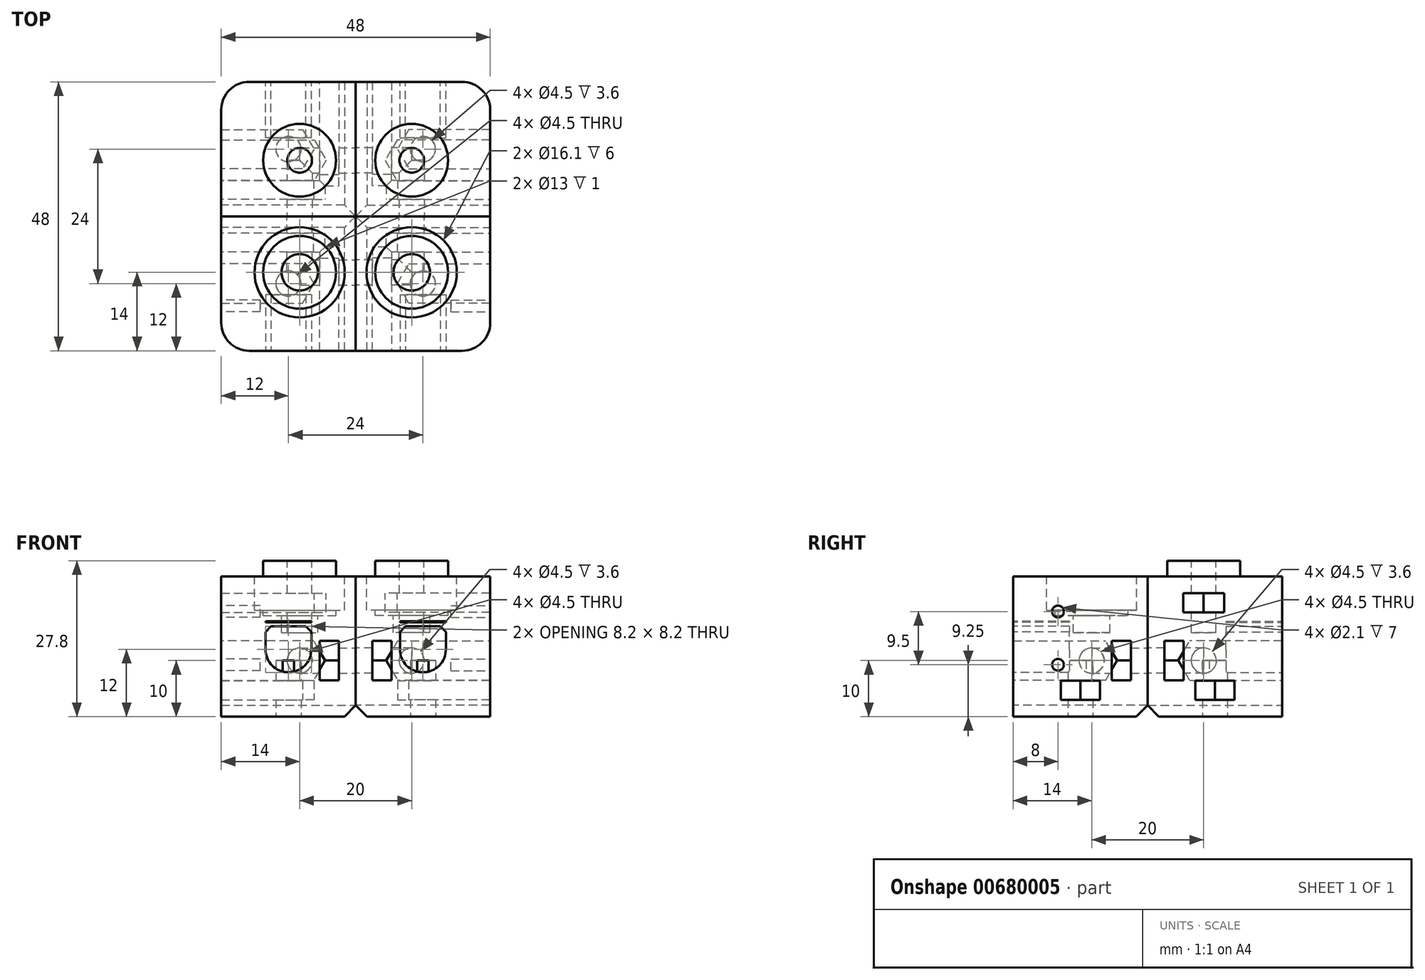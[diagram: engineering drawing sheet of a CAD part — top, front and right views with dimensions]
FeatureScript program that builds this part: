
annotation { "Feature Type Name" : "Feature", "Feature Type Description" : "" }
export const myFeature = defineFeature(function(context is Context, id is Id, definition is map)
    precondition{}
    {
        {
            var Q0;
            Q0=qCreatedBy(makeId("Top.planeOp"),FACE);
            var sketch = newSketch(context, id + "F0", { "sketchPlane" : qUnion([Q0])});
            skLineSegment(sketch, "E0.bottom", {"start": v(0, 0) * mm, "end": v(24, 0) * mm});
            skLineSegment(sketch, "E0.top", {"start": v(0, -24) * mm, "end": v(24, -24) * mm});
            skLineSegment(sketch, "E0.left", {"start": v(0, 0) * mm, "end": v(0, -24) * mm});
            skLineSegment(sketch, "E0.right", {"start": v(24, 0) * mm, "end": v(24, -24) * mm});
            skCircle(sketch, "E1", {"center": v(12, -12) * mm, "radius": 2.25 * mm});
            skLineSegment(sketch, "E2.3", {"start": v(9.48, -15.5) * mm, "end": v(7.46, -12) * mm});
            skLineSegment(sketch, "E2.4", {"start": v(7.46, -12) * mm, "end": v(9.48, -8.5) * mm});
            skLineSegment(sketch, "E3", {"start": v(24, -8.5) * mm, "end": v(24, -15.5) * mm});
            skLineSegment(sketch, "E4", {"start": v(9.48, -8.5) * mm, "end": v(24, -8.5) * mm});
            skLineSegment(sketch, "E5", {"start": v(24, -15.5) * mm, "end": v(9.48, -15.5) * mm});
            skLineSegment(sketch, "E6", {"start": v(8.47, -13.75) * mm, "end": v(11.5, -12) * mm, "construction": true});
            skLineSegment(sketch, "E7", {"start": v(11.5, -12) * mm, "end": v(12, -12) * mm, "construction": true});
            skLineSegment(sketch, "E8", {"start": v(7.46, -12) * mm, "end": v(11.5, -12) * mm, "construction": true});
            skSolve(sketch);
        }
        {
            var Q0;
            Q0=qSketchRegion(id+"F0",true);
            var Q1;
            Q1=makeQuery(id+"F0.imprint","IMPRINT",FACE,{"disambiguationData":[TD([[makeQuery(id+"F0.imprint","IMPRINT",EDGE,{"derivedFrom":sQuery(id+"F0.wireOp",EDGE,"E1")}),-1.0]])]});
            var Q2;
            Q2=makeQuery(id+"F0.imprint","IMPRINT",FACE,{"disambiguationData":[TD([[makeQuery(id+"F0.imprint","IMPRINT",EDGE,{"derivedFrom":sQuery(id+"F0.wireOp",EDGE,"E1")}),1.0]])]});
            extrude(context, id + "F1", {"entities" : qUnion([Q0, Q1, Q2]), "depth" : 25 * mm});
        }
        {
            var Q0;
            Q0=makeQuery(id+"F0.imprint","IMPRINT",FACE,{"disambiguationData":[TD([[makeQuery(id+"F0.imprint","IMPRINT",EDGE,{"derivedFrom":sQuery(id+"F0.wireOp",EDGE,"E1")}),1.0]])]});
            extrude(context, id + "F2", {"entities" : qUnion([Q0]), "operationType" : NewBodyOperationType.REMOVE, "depth" : 10 * mm});
        }
        {
            var Q0;
            Q0=makeQuery(id+"F0.imprint","IMPRINT",FACE,{"disambiguationData":[TD([[makeQuery(id+"F0.imprint","IMPRINT",EDGE,{"derivedFrom":sQuery(id+"F0.wireOp",EDGE,"E2.0")}),1.0]])]});
            var Q1;
            Q1=makeQuery(id+"F0.imprint","IMPRINT",FACE,{"disambiguationData":[TD([[makeQuery(id+"F0.imprint","IMPRINT",EDGE,{"derivedFrom":sQuery(id+"F0.wireOp",EDGE,"E1")}),-1.0]])]});
            extrude(context, id + "F3", {"entities" : qUnion([Q0, Q1]), "operationType" : NewBodyOperationType.REMOVE, "depth" : 3 * mm + 3.4 * mm});
        }
        {
            var Q0;
            Q0=makeQuery(id+"F0.imprint","IMPRINT",FACE,{"disambiguationData":[TD([[makeQuery(id+"F0.imprint","IMPRINT",EDGE,{"derivedFrom":sQuery(id+"F0.wireOp",EDGE,"E1")}),-1.0]])]});
            var Q1;
            Q1=makeQuery(id+"F0.imprint","IMPRINT",FACE,{"disambiguationData":[TD([[makeQuery(id+"F0.imprint","IMPRINT",EDGE,{"derivedFrom":sQuery(id+"F0.wireOp",EDGE,"E2.0")}),1.0]])]});
            extrude(context, id + "F4", {"entities" : qUnion([Q0, Q1]), "operationType" : NewBodyOperationType.ADD, "depth" : 3 * mm});
        }
        {
            var Q0;
            Q0=makeQuery(id+"F1.opExtrude","SWEPT_FACE",FACE,{"disambiguationData":[OSD([sQuery(id+"F0.wireOp",EDGE,"E0.top")])]});
            var sketch = newSketch(context, id + "F5", { "sketchPlane" : qUnion([Q0])});
            skCircle(sketch, "E9", {"center": v(12, 12) * mm, "radius": 4 * mm});
            skLineSegment(sketch, "E10", {"start": v(8.72, 14.3) * mm, "end": v(10.76, 17.2) * mm});
            skLineSegment(sketch, "E11", {"start": v(10.76, 17.2) * mm, "end": v(13.24, 17.2) * mm});
            skLineSegment(sketch, "E12", {"start": v(13.24, 17.2) * mm, "end": v(15.28, 14.3) * mm});
            skSolve(sketch);
        }
        {
            var Q0;
            {var subQ1=sQuery(id+"F5.wireOp",EDGE,"E10");Q0=makeQuery(id+"F5.imprint","IMPRINT",FACE,{"disambiguationData":[TD([[makeQuery(id+"F5.imprint","IMPRINT",EDGE,{"derivedFrom":subQ1}),1.0]])]});}
            var sketch = newSketch(context, id + "F6", { "sketchPlane" : qUnion([Q0])});
            skCircle(sketch, "E13", {"center": v(12, 12) * mm, "radius": 4.1 * mm});
            skLineSegment(sketch, "E14", {"start": v(16.1, 12) * mm, "end": v(16.1, 16.1) * mm, "construction": true});
            skLineSegment(sketch, "E15", {"start": v(16.1, 16.1) * mm, "end": v(7.9, 16.1) * mm});
            skLineSegment(sketch, "E16", {"start": v(7.9, 16.1) * mm, "end": v(7.9, 12) * mm, "construction": true});
            skLineSegment(sketch, "E17", {"start": v(7.9, 16.1) * mm, "end": v(7.9, 17) * mm, "construction": true});
            skLineSegment(sketch, "E18", {"start": v(7.9, 17) * mm, "end": v(7.9, 16.8) * mm});
            skLineSegment(sketch, "E19", {"start": v(7.9, 16.8) * mm, "end": v(16.1, 16.8) * mm});
            skLineSegment(sketch, "E20", {"start": v(16.1, 16.8) * mm, "end": v(16.1, 17) * mm});
            skLineSegment(sketch, "E21", {"start": v(16.1, 17) * mm, "end": v(7.9, 17) * mm});
            skLineSegment(sketch, "E22", {"start": v(15.1, 16.1) * mm, "end": v(16.1, 15.1) * mm});
            skLineSegment(sketch, "E23", {"start": v(16.1, 15.1) * mm, "end": v(16.1, 12) * mm});
            skLineSegment(sketch, "E24", {"start": v(7.9, 12) * mm, "end": v(7.9, 15.1) * mm});
            skLineSegment(sketch, "E25", {"start": v(7.9, 15.1) * mm, "end": v(8.9, 16.1) * mm});
            skSolve(sketch);
        }
        {
            var Q0;
            Q0=qSketchRegion(id+"F6",true);
            extrude(context, id + "F7", {"entities" : qUnion([Q0]), "operationType" : NewBodyOperationType.REMOVE, "oppositeDirection" : true, "depth" : 10 * mm});
        }
        {
            var Q0;
            Q0=makeQuery(id+"F1.opExtrude","SWEPT_FACE",FACE,{"disambiguationData":[OSD([sQuery(id+"F0.wireOp",EDGE,"E0.left")])]});
            var sketch = newSketch(context, id + "F8", { "sketchPlane" : qUnion([Q0])});
            skCircle(sketch, "E26", {"center": v(10, 10) * mm, "radius": 2.25 * mm});
            skLineSegment(sketch, "E27.3", {"start": v(7.48, 6.5) * mm, "end": v(5.46, 10) * mm});
            skLineSegment(sketch, "E27.4", {"start": v(5.46, 10) * mm, "end": v(7.48, 13.5) * mm});
            skLineSegment(sketch, "E28", {"start": v(24, 6.5) * mm, "end": v(24, 13.5) * mm});
            skLineSegment(sketch, "E29", {"start": v(24, 13.5) * mm, "end": v(7.48, 13.5) * mm});
            skLineSegment(sketch, "E30", {"start": v(7.48, 6.5) * mm, "end": v(24, 6.5) * mm});
            skLineSegment(sketch, "E31", {"start": v(10, 13.5) * mm, "end": v(10, 6.5) * mm, "construction": true});
            skLineSegment(sketch, "E32", {"start": v(6.47, 11.75) * mm, "end": v(9.5, 10) * mm, "construction": true});
            skLineSegment(sketch, "E33", {"start": v(9.5, 10) * mm, "end": v(10, 10) * mm, "construction": true});
            skSolve(sketch);
        }
        {
            var Q0;
            Q0=makeQuery(id+"F8.imprint","IMPRINT",FACE,{"disambiguationData":[TD([[makeQuery(id+"F8.imprint","IMPRINT",EDGE,{"derivedFrom":sQuery(id+"F8.wireOp",EDGE,"E26")}),1.0]])]});
            extrude(context, id + "F9", {"entities" : qUnion([Q0]), "operationType" : NewBodyOperationType.REMOVE, "oppositeDirection" : true, "depth" : 10 * mm});
        }
        {
            var Q0;
            Q0=makeQuery(id+"F8.imprint","IMPRINT",FACE,{"disambiguationData":[TD([[makeQuery(id+"F8.imprint","IMPRINT",EDGE,{"derivedFrom":sQuery(id+"F8.wireOp",EDGE,"E26")}),-1.0]])]});
            var Q1;
            Q1=makeQuery(id+"F8.imprint","IMPRINT",FACE,{"disambiguationData":[TD([[makeQuery(id+"F8.imprint","IMPRINT",EDGE,{"derivedFrom":sQuery(id+"F8.wireOp",EDGE,"E27.0")}),1.0]])]});
            extrude(context, id + "F10", {"entities" : qUnion([Q0, Q1]), "operationType" : NewBodyOperationType.REMOVE, "oppositeDirection" : true, "depth" : 3 * mm + 3.4 * mm});
        }
        {
            var Q0;
            Q0=makeQuery(id+"F8.imprint","IMPRINT",FACE,{"disambiguationData":[TD([[makeQuery(id+"F8.imprint","IMPRINT",EDGE,{"derivedFrom":sQuery(id+"F8.wireOp",EDGE,"E26")}),-1.0]])]});
            var Q1;
            Q1=makeQuery(id+"F8.imprint","IMPRINT",FACE,{"disambiguationData":[TD([[makeQuery(id+"F8.imprint","IMPRINT",EDGE,{"derivedFrom":sQuery(id+"F8.wireOp",EDGE,"E27.0")}),1.0]])]});
            extrude(context, id + "F11", {"entities" : qUnion([Q0, Q1]), "operationType" : NewBodyOperationType.ADD, "oppositeDirection" : true, "depth" : 3 * mm});
        }
        {
            var Q0;
            Q0=makeQuery(id+"F1.opExtrude","SWEPT_FACE",FACE,{"disambiguationData":[OSD([sQuery(id+"F0.wireOp",EDGE,"E0.bottom")])]});
            var sketch = newSketch(context, id + "F12", { "sketchPlane" : qUnion([Q0])});
            skCircle(sketch, "E34", {"center": v(-10, 10) * mm, "radius": 2.25 * mm});
            skLineSegment(sketch, "E35.0", {"start": v(-7.48, 13.5) * mm, "end": v(-5.46, 10) * mm});
            skLineSegment(sketch, "E35.1", {"start": v(-5.46, 10) * mm, "end": v(-7.48, 6.5) * mm});
            skPoint(sketch, "E35.0.midPoint", {"position": v(-6.47, 11.75) * mm});
            skLineSegment(sketch, "E36", {"start": v(-24, 13.5) * mm, "end": v(-24, 6.5) * mm});
            skLineSegment(sketch, "E37", {"start": v(-7.48, 13.5) * mm, "end": v(-24, 13.5) * mm});
            skLineSegment(sketch, "E38", {"start": v(-24, 6.5) * mm, "end": v(-7.48, 6.5) * mm});
            skLineSegment(sketch, "E39", {"start": v(-10, 13.5) * mm, "end": v(-10, 6.5) * mm, "construction": true});
            skLineSegment(sketch, "E40", {"start": v(-6.47, 11.75) * mm, "end": v(-9.5, 10) * mm});
            skLineSegment(sketch, "E41", {"start": v(-9.5, 10) * mm, "end": v(-10, 10) * mm});
            skSolve(sketch);
        }
        {
            var Q0;
            Q0=makeQuery(id+"F12.imprint","IMPRINT",FACE,{"disambiguationData":[TD([[makeQuery(id+"F12.imprint","IMPRINT",EDGE,{"derivedFrom":sQuery(id+"F12.wireOp",EDGE,"E34")}),1.0]])]});
            extrude(context, id + "F13", {"entities" : qUnion([Q0]), "operationType" : NewBodyOperationType.REMOVE, "oppositeDirection" : true, "depth" : 10 * mm});
        }
        {
            var Q0;
            Q0=makeQuery(id+"F12.imprint","IMPRINT",FACE,{"disambiguationData":[TD([[makeQuery(id+"F12.imprint","IMPRINT",EDGE,{"derivedFrom":sQuery(id+"F12.wireOp",EDGE,"E35.3")}),1.0]])]});
            var Q1;
            Q1=makeQuery(id+"F12.imprint","IMPRINT",FACE,{"disambiguationData":[TD([[makeQuery(id+"F12.imprint","IMPRINT",EDGE,{"derivedFrom":sQuery(id+"F12.wireOp",EDGE,"E34")}),-1.0]])]});
            extrude(context, id + "F14", {"entities" : qUnion([Q0, Q1]), "operationType" : NewBodyOperationType.REMOVE, "oppositeDirection" : true, "depth" : 3 * mm + 3.4 * mm});
        }
        {
            var Q0;
            Q0=makeQuery(id+"F12.imprint","IMPRINT",FACE,{"disambiguationData":[TD([[makeQuery(id+"F12.imprint","IMPRINT",EDGE,{"derivedFrom":sQuery(id+"F12.wireOp",EDGE,"E35.3")}),1.0]])]});
            var Q1;
            Q1=makeQuery(id+"F12.imprint","IMPRINT",FACE,{"disambiguationData":[TD([[makeQuery(id+"F12.imprint","IMPRINT",EDGE,{"derivedFrom":sQuery(id+"F12.wireOp",EDGE,"E34")}),-1.0]])]});
            extrude(context, id + "F15", {"entities" : qUnion([Q0, Q1]), "operationType" : NewBodyOperationType.ADD, "oppositeDirection" : true, "depth" : 3 * mm});
        }
        {
            var Q0;
            Q0=makeQuery(id+"F1.opExtrude","SWEPT_EDGE",EDGE,{"disambiguationData":[OSD([sQuery(id+"F0.wireOp",EDGE,"E0.top"),sQuery(id+"F0.wireOp",EDGE,"E0.right")])]});
            fillet(context, id + "F16", {"entities" : qUnion([Q0]), "radius" : 5 * mm, "tangentPropagation" : true, "allowEdgeOverflow" : false});
        }
        {
            var Q0;
            Q0=makeQuery(id+"F1.opExtrude","CAP_EDGE",EDGE,{"disambiguationData":[OSD([sQuery(id+"F0.wireOp",EDGE,"E0.left")])],"isStart":true});
            var Q1;
            Q1=makeQuery(id+"F1.opExtrude","CAP_EDGE",EDGE,{"disambiguationData":[OSD([sQuery(id+"F0.wireOp",EDGE,"E0.bottom")])],"isStart":true});
            chamfer(context, id + "F17", {"entities" : qUnion([Q0, Q1]), "width" : 2 * mm, "tangentPropagation" : true});
        }
        {
            var Q0;
            Q0=makeQuery(id+"F1.opExtrude","SWEPT_BODY",BODY,{"disambiguationData":[OSD([sQuery(id+"F0.wireOp",EDGE,"E0.bottom"),sQuery(id+"F0.wireOp",EDGE,"E0.top"),sQuery(id+"F0.wireOp",EDGE,"E0.left"),sQuery(id+"F0.wireOp",EDGE,"E0.right"),sQuery(id+"F0.wireOp",EDGE,"E3")])]});
            var Q1;
            Q1=qCreatedBy(makeId("Front.planeOp"),FACE);
            mirror(context, id + "F18", {"entities" : qUnion([Q0]), "mirrorPlane" : qUnion([Q1])});
        }
        {
            var Q0;
            Q0=makeQuery(id+"F18.opPattern","COPY",FACE,{"derivedFrom":makeQuery(id+"F1.opExtrude","CAP_FACE",FACE,{"disambiguationData":[OSD([sQuery(id+"F0.wireOp",EDGE,"E0.bottom"),sQuery(id+"F0.wireOp",EDGE,"E0.top"),sQuery(id+"F0.wireOp",EDGE,"E0.left"),sQuery(id+"F0.wireOp",EDGE,"E0.right"),sQuery(id+"F0.wireOp",EDGE,"E3")])],"isStart":false}),"instanceName":"1"});
            var sketch = newSketch(context, id + "F19", { "sketchPlane" : qUnion([Q0])});
            skCircle(sketch, "E42", {"center": v(10, 10) * mm, "radius": 2.2 * mm});
            skCircle(sketch, "E43", {"center": v(10, 10) * mm, "radius": 6.5 * mm});
            skLineSegment(sketch, "E44", {"start": v(24, 13.65) * mm, "end": v(24, 6.35) * mm});
            skLineSegment(sketch, "E45", {"start": v(24, 13.65) * mm, "end": v(7.4, 13.65) * mm});
            skLineSegment(sketch, "E46", {"start": v(7.4, 13.65) * mm, "end": v(5.29, 10) * mm});
            skLineSegment(sketch, "E47", {"start": v(5.29, 10) * mm, "end": v(7.4, 6.35) * mm});
            skLineSegment(sketch, "E48", {"start": v(7.4, 6.35) * mm, "end": v(24, 6.35) * mm});
            skLineSegment(sketch, "E49", {"start": v(6.34, 11.83) * mm, "end": v(9.5, 10) * mm, "construction": true});
            skLineSegment(sketch, "E50", {"start": v(9.5, 10) * mm, "end": v(10, 10) * mm, "construction": true});
            skLineSegment(sketch, "E51", {"start": v(5.29, 10) * mm, "end": v(9.5, 10) * mm, "construction": true});
            skSolve(sketch);
        }
        {
            var Q0;
            Q0=makeQuery(id+"F19.imprint","IMPRINT",FACE,{"disambiguationData":[TD([[makeQuery(id+"F19.imprint","IMPRINT",EDGE,{"derivedFrom":sQuery(id+"F19.wireOp",EDGE,"E42")}),1.0]])]});
            extrude(context, id + "F20", {"entities" : qUnion([Q0]), "operationType" : NewBodyOperationType.REMOVE, "oppositeDirection" : true, "depth" : 10 * mm});
        }
        {
            var Q0;
            {var subQ6=sQuery(id+"F19.wireOp",EDGE,"3c2f8247-9d55-409e-9478-93798bc3c1df.1");Q0=makeQuery(id+"F19.imprint","IMPRINT",FACE,{"disambiguationData":[TD([[makeQuery(id+"F19.imprint","IMPRINT",EDGE,{"derivedFrom":subQ6}),1.0]])]});}
            var Q1;
            {var subQ4=sQuery(id+"F19.wireOp",EDGE,"E44");Q1=makeQuery(id+"F19.imprint","IMPRINT",FACE,{"disambiguationData":[TD([[makeQuery(id+"F19.imprint","IMPRINT",EDGE,{"derivedFrom":subQ4}),1.0]])]});}
            var Q2;
            Q2=makeQuery(id+"F19.imprint","IMPRINT",FACE,{"disambiguationData":[TD([[makeQuery(id+"F19.imprint","IMPRINT",EDGE,{"derivedFrom":sQuery(id+"F19.wireOp",EDGE,"E42")}),-1.0]])]});
            extrude(context, id + "F21", {"entities" : qUnion([Q0, Q1, Q2]), "operationType" : NewBodyOperationType.REMOVE, "oppositeDirection" : true, "depth" : 3 * mm + 3.4 * mm});
        }
        {
            var Q0;
            Q0=makeQuery(id+"F19.imprint","IMPRINT",FACE,{"disambiguationData":[TD([[makeQuery(id+"F19.imprint","IMPRINT",EDGE,{"derivedFrom":sQuery(id+"F19.wireOp",EDGE,"E42")}),-1.0]])]});
            var Q1;
            {var subQ4=sQuery(id+"F19.wireOp",EDGE,"E44");Q1=makeQuery(id+"F19.imprint","IMPRINT",FACE,{"disambiguationData":[TD([[makeQuery(id+"F19.imprint","IMPRINT",EDGE,{"derivedFrom":subQ4}),1.0]])]});}
            var Q2;
            {var subQ6=sQuery(id+"F19.wireOp",EDGE,"3c2f8247-9d55-409e-9478-93798bc3c1df.1");Q2=makeQuery(id+"F19.imprint","IMPRINT",FACE,{"disambiguationData":[TD([[makeQuery(id+"F19.imprint","IMPRINT",EDGE,{"derivedFrom":subQ6}),1.0]])]});}
            extrude(context, id + "F22", {"entities" : qUnion([Q0, Q1, Q2]), "operationType" : NewBodyOperationType.ADD, "oppositeDirection" : true, "depth" : 3 * mm});
        }
        {
            var Q0;
            {var subQ4=sQuery(id+"F19.wireOp",EDGE,"E46");Q0=makeQuery(id+"F19.imprint","IMPRINT",FACE,{"disambiguationData":[TD([[makeQuery(id+"F19.imprint","IMPRINT",EDGE,{"derivedFrom":subQ4}),-1.0]])]});}
            var Q1;
            Q1=makeQuery(id+"F19.imprint","IMPRINT",FACE,{"disambiguationData":[TD([[makeQuery(id+"F19.imprint","IMPRINT",EDGE,{"derivedFrom":sQuery(id+"F19.wireOp",EDGE,"E42")}),-1.0]])]});
            extrude(context, id + "F23", {"entities" : qUnion([Q0, Q1]), "operationType" : NewBodyOperationType.ADD, "depth" : 16 * mm + 12 * mm - 25 * mm - .2 * mm});
        }
        {
            var Q0;
            Q0=makeQuery(id+"F1.opExtrude","CAP_FACE",FACE,{"disambiguationData":[OSD([sQuery(id+"F0.wireOp",EDGE,"E0.bottom"),sQuery(id+"F0.wireOp",EDGE,"E0.top"),sQuery(id+"F0.wireOp",EDGE,"E0.left"),sQuery(id+"F0.wireOp",EDGE,"E0.right")])],"isStart":false});
            var sketch = newSketch(context, id + "F24", { "sketchPlane" : qUnion([Q0])});
            skCircle(sketch, "E52", {"center": v(10, -10) * mm, "radius": 3.25 * mm});
            skCircle(sketch, "E53", {"center": v(10, -10) * mm, "radius": 8.05 * mm});
            skCircle(sketch, "E54", {"center": v(10, -10) * mm, "radius": 6.5 * mm});
            skSolve(sketch);
        }
        {
            var Q0;
            Q0=makeQuery(id+"F24.imprint","IMPRINT",FACE,{"disambiguationData":[TD([[makeQuery(id+"F24.imprint","IMPRINT",EDGE,{"derivedFrom":sQuery(id+"F24.wireOp",EDGE,"E52")}),1.0]])]});
            extrude(context, id + "F25", {"entities" : qUnion([Q0]), "operationType" : NewBodyOperationType.REMOVE, "oppositeDirection" : true, "depth" : 10 * mm});
        }
        {
            var Q0;
            Q0=makeQuery(id+"F24.imprint","IMPRINT",FACE,{"disambiguationData":[TD([[makeQuery(id+"F24.imprint","IMPRINT",EDGE,{"derivedFrom":sQuery(id+"F24.wireOp",EDGE,"E52")}),-1.0]])]});
            var Q1;
            Q1=makeQuery(id+"F24.imprint","IMPRINT",FACE,{"disambiguationData":[TD([[makeQuery(id+"F24.imprint","IMPRINT",EDGE,{"derivedFrom":sQuery(id+"F24.wireOp",EDGE,"E53")}),1.0]])]});
            extrude(context, id + "F26", {"entities" : qUnion([Q0, Q1]), "operationType" : NewBodyOperationType.REMOVE, "oppositeDirection" : true, "depth" : 6 * mm});
        }
        {
            var Q0;
            Q0=makeQuery(id+"F24.imprint","IMPRINT",FACE,{"disambiguationData":[TD([[makeQuery(id+"F24.imprint","IMPRINT",EDGE,{"derivedFrom":sQuery(id+"F24.wireOp",EDGE,"E52")}),-1.0]])]});
            extrude(context, id + "F27", {"entities" : qUnion([Q0]), "operationType" : NewBodyOperationType.REMOVE, "oppositeDirection" : true, "depth" : 7 * mm});
        }
        {
            var Q0;
            {var subQ0=sQuery(id+"F0.wireOp",EDGE,"E3");Q0=makeQuery(id+"F15.boolean.opBoolean","MERGE",FACE,{"derivedFrom":[makeQuery(id+"F4.boolean.opBoolean","MERGE",FACE,{"derivedFrom":[makeQuery(id+"F1.opExtrude","SWEPT_FACE",FACE,{"disambiguationData":[OSD([sQuery(id+"F0.wireOp",EDGE,"E0.right"),subQ0])]}),makeQuery(id+"F4.opExtrude","SWEPT_FACE",FACE,{"disambiguationData":[OSD([subQ0])]})]}),makeQuery(id+"F15.opExtrude","SWEPT_FACE",FACE,{"disambiguationData":[OSD([sQuery(id+"F12.wireOp",EDGE,"E36")])]})]});}
            var sketch = newSketch(context, id + "F28", { "sketchPlane" : qUnion([Q0])});
            skLineSegment(sketch, "E55", {"start": v(-16, 18.75) * mm, "end": v(-16, 9.25) * mm, "construction": true});
            skCircle(sketch, "E56", {"center": v(-16, 18.75) * mm, "radius": 1.05 * mm});
            skCircle(sketch, "E57", {"center": v(-16, 9.25) * mm, "radius": 1.05 * mm});
            skPoint(sketch, "E58", {"position": v(-16, 14) * mm});
            skSolve(sketch);
        }
        {
            var Q0;
            Q0=qSketchRegion(id+"F28",true);
            extrude(context, id + "F29", {"entities" : qUnion([Q0]), "operationType" : NewBodyOperationType.REMOVE, "oppositeDirection" : true, "depth" : 7 * mm});
        }
        {
            var Q0;
            Q0=makeQuery(id+"F1.opExtrude","SWEPT_BODY",BODY,{"disambiguationData":[OSD([sQuery(id+"F0.wireOp",EDGE,"E0.bottom"),sQuery(id+"F0.wireOp",EDGE,"E0.top"),sQuery(id+"F0.wireOp",EDGE,"E0.left"),sQuery(id+"F0.wireOp",EDGE,"E0.right"),sQuery(id+"F0.wireOp",EDGE,"E3")])]});
            var Q1;
            Q1=qCreatedBy(makeId("Right.planeOp"),FACE);
            mirror(context, id + "F30", {"entities" : qUnion([Q0]), "mirrorPlane" : qUnion([Q1])});
        }
        {
            var Q0;
            Q0=makeQuery(id+"F18.opPattern","COPY",BODY,{"derivedFrom":makeQuery(id+"F1.opExtrude","SWEPT_BODY",BODY,{"disambiguationData":[OSD([sQuery(id+"F0.wireOp",EDGE,"E0.bottom"),sQuery(id+"F0.wireOp",EDGE,"E0.top"),sQuery(id+"F0.wireOp",EDGE,"E0.left"),sQuery(id+"F0.wireOp",EDGE,"E0.right"),sQuery(id+"F0.wireOp",EDGE,"E3")])]}),"instanceName":"1"});
            var Q1;
            Q1=qCreatedBy(makeId("Right.planeOp"),FACE);
            mirror(context, id + "F31", {"entities" : qUnion([Q0]), "mirrorPlane" : qUnion([Q1])});
        }
    });
